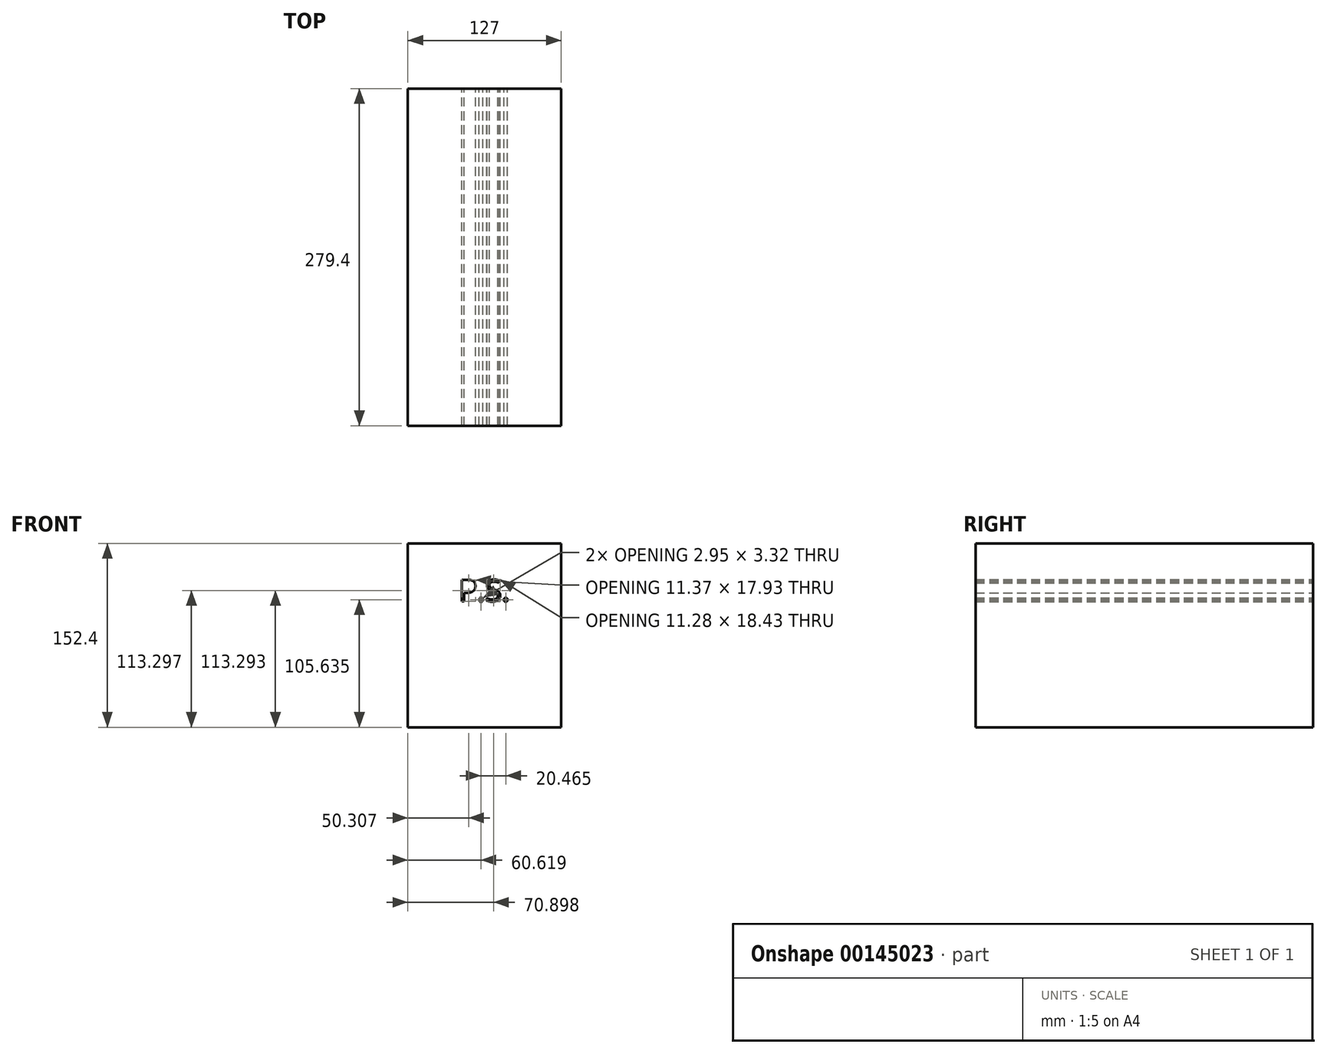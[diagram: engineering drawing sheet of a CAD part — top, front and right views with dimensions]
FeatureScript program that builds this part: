
annotation { "Feature Type Name" : "Feature", "Feature Type Description" : "" }
export const myFeature = defineFeature(function(context is Context, id is Id, definition is map)
    precondition{}
    {
        {
            var Q0;
            Q0=qCreatedBy(makeId("Front.planeOp"),FACE);
            var sketch = newSketch(context, id + "F0", { "sketchPlane" : qUnion([Q0])});
            skLineSegment(sketch, "E0.bottom", {"start": v(0, 0) * mm, "end": v(-127, 0) * mm});
            skLineSegment(sketch, "E0.top", {"start": v(0, 152.4) * mm, "end": v(-127, 152.4) * mm});
            skLineSegment(sketch, "E0.left", {"start": v(0, 0) * mm, "end": v(0, 152.4) * mm});
            skLineSegment(sketch, "E0.right", {"start": v(-127, 0) * mm, "end": v(-127, 152.4) * mm});
            skText(sketch, "E1", { "text": "P.S.", "fontName": "OpenSans-Regular.ttf"});
            const initialGuessF0  = {"E1": [-0.08484, 0.10433, 1, 0, 0.01808]};
            skSetInitialGuess(sketch, initialGuessF0);
            skSolve(sketch);
        }
        {
            var Q0;
            Q0=makeQuery(id+"F0.imprint","IMPRINT",FACE,{"disambiguationData":[TD([[makeQuery(id+"F0.imprint","IMPRINT",EDGE,{"derivedFrom":sQuery(id+"F0.wireOp",EDGE,"E0.bottom")}),-1.0]])]});
            extrude(context, id + "F1", {"entities" : qUnion([Q0]), "depth" : 279.4 * mm});
        }
    });
